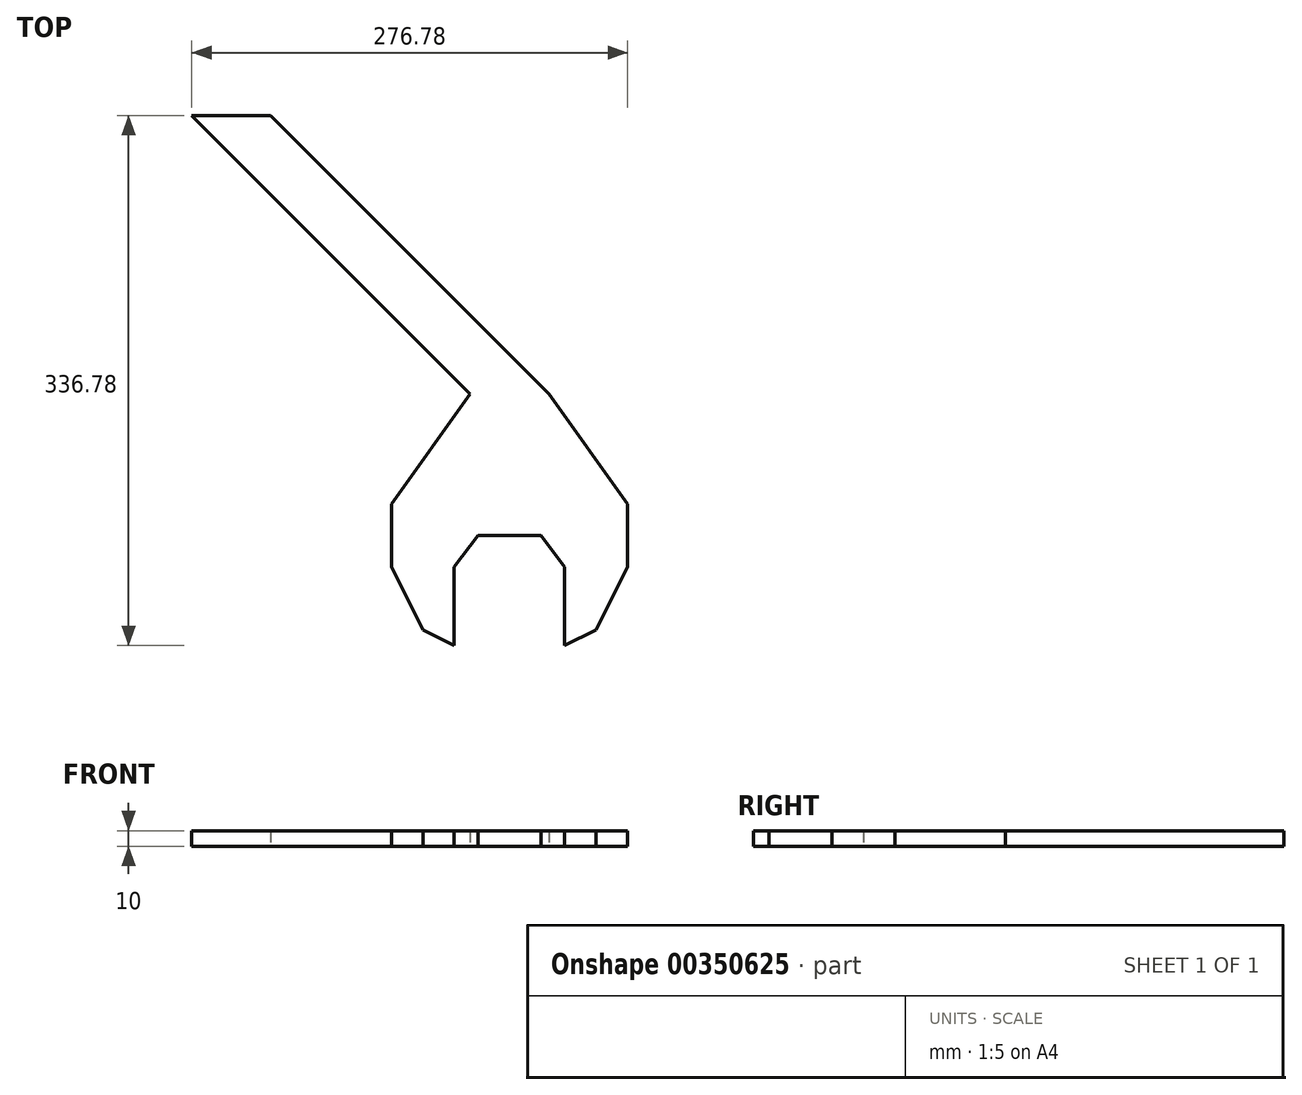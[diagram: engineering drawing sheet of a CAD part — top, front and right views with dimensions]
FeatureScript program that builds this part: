
annotation { "Feature Type Name" : "Feature", "Feature Type Description" : "" }
export const myFeature = defineFeature(function(context is Context, id is Id, definition is map)
    precondition{}
    {
        {
            var Q0;
            Q0=qCreatedBy(makeId("Top.planeOp"),FACE);
            var sketch = newSketch(context, id + "F0", { "sketchPlane" : qUnion([Q0])});
            skLineSegment(sketch, "E0", {"start": v(-20, 0) * mm, "end": v(20, 0) * mm});
            skLineSegment(sketch, "E1", {"start": v(-20, 0) * mm, "end": v(-35, -20) * mm});
            skLineSegment(sketch, "E2", {"start": v(-35, -20) * mm, "end": v(-35, -70) * mm});
            skLineSegment(sketch, "E3", {"start": v(0, 0) * mm, "end": v(0, -67.64) * mm, "construction": true});
            skLineSegment(sketch, "E4.MirrorCS", {"start": v(20, 0) * mm, "end": v(35, -20) * mm});
            skLineSegment(sketch, "E5.MirrorCS", {"start": v(35, -20) * mm, "end": v(35, -70) * mm});
            skLineSegment(sketch, "E6", {"start": v(-35, -70) * mm, "end": v(-55, -60) * mm});
            skLineSegment(sketch, "E7", {"start": v(-55, -60) * mm, "end": v(-75, -20) * mm});
            skLineSegment(sketch, "E8", {"start": v(-75, -20) * mm, "end": v(-75, 20) * mm});
            skLineSegment(sketch, "E9", {"start": v(-75, 20) * mm, "end": v(-25, 90) * mm});
            skLineSegment(sketch, "E10.MirrorCS", {"start": v(35, -70) * mm, "end": v(55, -60) * mm});
            skLineSegment(sketch, "E11.MirrorCS", {"start": v(55, -60) * mm, "end": v(75, -20) * mm});
            skLineSegment(sketch, "E12.MirrorCS", {"start": v(75, 20) * mm, "end": v(25, 90) * mm});
            skLineSegment(sketch, "E13.MirrorCS", {"start": v(75, -20) * mm, "end": v(75, 20) * mm});
            skLineSegment(sketch, "E14", {"start": v(-25, 90) * mm, "end": v(-201.78, 266.78) * mm});
            skLineSegment(sketch, "E15", {"start": v(-201.78, 266.78) * mm, "end": v(-151.78, 266.78) * mm});
            skLineSegment(sketch, "E16", {"start": v(-151.78, 266.78) * mm, "end": v(25, 90) * mm});
            skLineSegment(sketch, "E17", {"start": v(25, 90) * mm, "end": v(157.59, 90) * mm, "construction": true});
            skSolve(sketch);
        }
        {
            var Q0;
            Q0=makeQuery(id+"F0.imprint","IMPRINT",FACE,{"disambiguationData":[TD([[makeQuery(id+"F0.imprint","IMPRINT",EDGE,{"derivedFrom":sQuery(id+"F0.wireOp",EDGE,"E0")}),1.0]])]});
            extrude(context, id + "F1", {"entities" : qUnion([Q0]), "depth" : 10 * mm});
        }
    });
